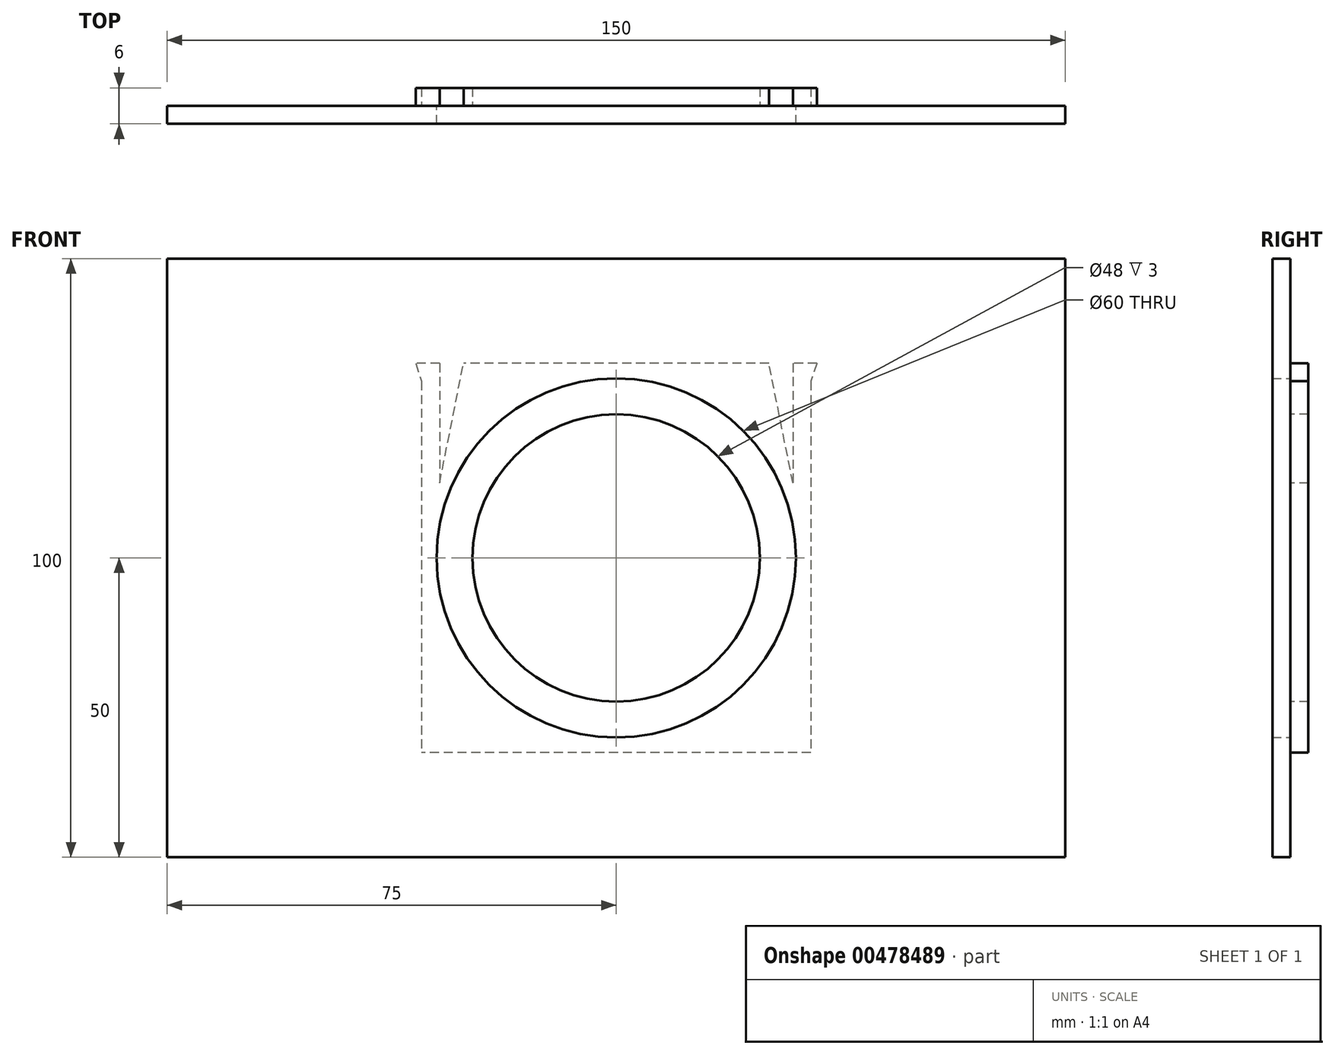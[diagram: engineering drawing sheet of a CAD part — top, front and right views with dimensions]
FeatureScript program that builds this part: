
annotation { "Feature Type Name" : "Feature", "Feature Type Description" : "" }
export const myFeature = defineFeature(function(context is Context, id is Id, definition is map)
    precondition{}
    {
        {
            var Q0;
            Q0=qCreatedBy(makeId("Front.planeOp"),FACE);
            var sketch = newSketch(context, id + "F0", { "sketchPlane" : qUnion([Q0])});
            skCircle(sketch, "E0", {"center": v(0, 0) * mm, "radius": 30 * mm});
            skLineSegment(sketch, "E1.bottom", {"start": v(-75, 50) * mm, "end": v(75, 50) * mm});
            skLineSegment(sketch, "E1.top", {"start": v(-75, -50) * mm, "end": v(75, -50) * mm});
            skLineSegment(sketch, "E1.left", {"start": v(-75, 50) * mm, "end": v(-75, -50) * mm});
            skLineSegment(sketch, "E1.right", {"start": v(75, 50) * mm, "end": v(75, -50) * mm});
            skSolve(sketch);
        }
        {
            var Q0;
            Q0=makeQuery(id+"F0.imprint","IMPRINT",FACE,{"disambiguationData":[TD([[makeQuery(id+"F0.imprint","IMPRINT",EDGE,{"derivedFrom":sQuery(id+"F0.wireOp",EDGE,"E0")}),-1.0]])]});
            extrude(context, id + "F1", {"entities" : qUnion([Q0]), "depth" : 3 * mm});
        }
        {
            var Q0;
            Q0=makeQuery(id+"F1.opExtrude","CAP_FACE",FACE,{"disambiguationData":[OSD([sQuery(id+"F0.wireOp",EDGE,"E0"),sQuery(id+"F0.wireOp",EDGE,"E1.bottom"),sQuery(id+"F0.wireOp",EDGE,"E1.top"),sQuery(id+"F0.wireOp",EDGE,"E1.left"),sQuery(id+"F0.wireOp",EDGE,"E1.right")])],"isStart":true});
            var sketch = newSketch(context, id + "F2", { "sketchPlane" : qUnion([Q0])});
            skCircle(sketch, "E2", {"center": v(0, 0) * mm, "radius": 24 * mm});
            skLineSegment(sketch, "E3.bottom", {"start": v(-32.5, 32.5) * mm, "end": v(-29.5, 32.5) * mm});
            skLineSegment(sketch, "E3.top", {"start": v(-32.5, -32.5) * mm, "end": v(-29.5, -32.5) * mm});
            skLineSegment(sketch, "E3.left", {"start": v(-32.5, 29.5) * mm, "end": v(-32.5, -32.5) * mm});
            skLineSegment(sketch, "E3.right", {"start": v(32.5, 29.5) * mm, "end": v(32.5, -32.5) * mm});
            skLineSegment(sketch, "E4", {"start": v(-32.5, -32.5) * mm, "end": v(-29.5, -32.5) * mm, "construction": true});
            skLineSegment(sketch, "E5.trimOffspring", {"start": v(-25.5, -32.5) * mm, "end": v(32.5, -32.5) * mm});
            skLineSegment(sketch, "E6", {"start": v(-16.17, 0) * mm, "end": v(16.21, 0) * mm, "construction": true});
            skLineSegment(sketch, "E7.MirrorCS", {"start": v(-29.5, 32.5) * mm, "end": v(-29.5, 12.5) * mm});
            skLineSegment(sketch, "E8.MirrorCS", {"start": v(-29.5, 12.5) * mm, "end": v(-25.5, 32.5) * mm});
            skLineSegment(sketch, "E9.MirrorCS", {"start": v(-32.5, 32.5) * mm, "end": v(-29.5, 32.5) * mm, "construction": true});
            skLineSegment(sketch, "E10.trimOffspring", {"start": v(-25.5, 32.5) * mm, "end": v(25.5, 32.5) * mm});
            skLineSegment(sketch, "E11", {"start": v(-25.5, -32.5) * mm, "end": v(-29.5, -32.5) * mm});
            skLineSegment(sketch, "E12", {"start": v(0, 17.09) * mm, "end": v(0, -14.8) * mm, "construction": true});
            skLineSegment(sketch, "E13.MirrorCS", {"start": v(29.5, 32.5) * mm, "end": v(29.5, 12.5) * mm});
            skLineSegment(sketch, "E14.MirrorCS", {"start": v(29.5, 12.5) * mm, "end": v(25.5, 32.5) * mm});
            skLineSegment(sketch, "E15.trimOffspring", {"start": v(29.5, 32.5) * mm, "end": v(32.5, 32.5) * mm});
            skLineSegment(sketch, "E16", {"start": v(32.5, 32.5) * mm, "end": v(33.5, 32.5) * mm});
            skLineSegment(sketch, "E17", {"start": v(33.5, 32.5) * mm, "end": v(32.5, 29.5) * mm});
            skLineSegment(sketch, "E18.MirrorCS", {"start": v(-32.5, 32.5) * mm, "end": v(-33.5, 32.5) * mm});
            skLineSegment(sketch, "E19.MirrorCS", {"start": v(-33.5, 32.5) * mm, "end": v(-32.5, 29.5) * mm});
            skSolve(sketch);
        }
        {
            var Q0;
            Q0=makeQuery(id+"F2.imprint","IMPRINT",FACE,{"disambiguationData":[TD([[makeQuery(id+"F2.imprint","IMPRINT",EDGE,{"derivedFrom":sQuery(id+"F2.wireOp",EDGE,"E3.bottom")}),-1.0]])]});
            var Q1;
            Q1=makeQuery(id+"F2.imprint","IMPRINT",FACE,{"disambiguationData":[TD([[makeQuery(id+"F2.imprint","IMPRINT",EDGE,{"derivedFrom":sQuery(id+"F2.wireOp",EDGE,"E2")}),-1.0]])]});
            extrude(context, id + "F3", {"entities" : qUnion([Q0, Q1]), "depth" : 3 * mm});
        }
    });
